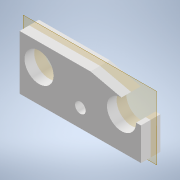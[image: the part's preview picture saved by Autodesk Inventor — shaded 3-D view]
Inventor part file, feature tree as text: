
AUTODESK INVENTOR PART (.ipt)
format: ipt  version: 2022.3 (Build 263350000, 350)  size: 139,264 bytes
history: native  units: mm
features: other x5, extrude x3, sketch x3, reference x2, plane x1, projected_geometry x1
ambient origin geometry x8: Origin, YZ Plane, XZ Plane, XY Plane, X Axis, Y Axis, Z Axis, Center Point
bodies: Solid1 (feature_tree)
feature tree (15):
  plane  "Work Plane1"
  extrude  "Extrusion1"  Depth=4.0mm TaperAngle=0.0deg
  extrude  "Extrusion2"  Depth=0.5mm
  extrude  "Extrusion3"  [1 undecoded]
  sketch  "Sketch1"  dims[d0=2.2mm d1=4.0mm d2=0.0mm]
  reference  "Reference1"
  sketch  "Sketch2"  dims[d3=4.0mm d4=0.0mm d5=0.5mm]
  reference  "Reference2"
  sketch  "Sketch3"  dims[d6=10.0mm d7=0.0mm]
  projected_geometry  "Projected Loop1"
  other  "<userpath>\Documents\Inventor\NanoSumo\NanoSumo_part1.iam"
  other  "NanoSumo_part1.iam"
  other  "bok:2"
  other  "bok:1"
  other  "Assembly3"
note: 1 required parameter value undecoded (feature->parameter linkage not recoverable at this tier; creation-order binding heuristic only, values carry confidence <= 0.55)
